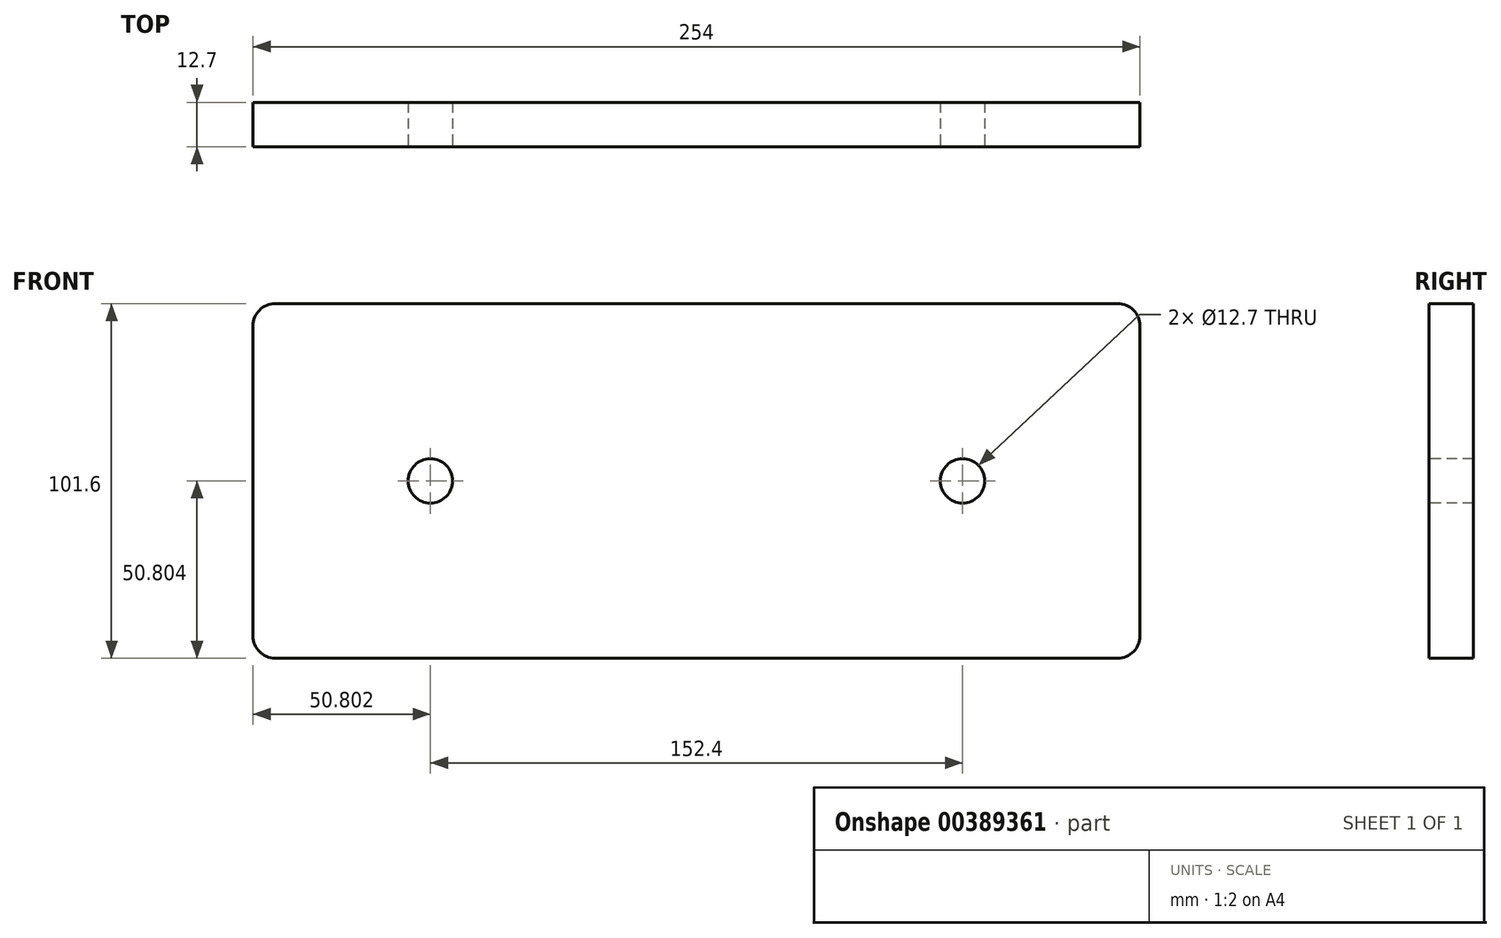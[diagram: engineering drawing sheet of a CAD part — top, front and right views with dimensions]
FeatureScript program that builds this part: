
annotation { "Feature Type Name" : "Feature", "Feature Type Description" : "" }
export const myFeature = defineFeature(function(context is Context, id is Id, definition is map)
    precondition{}
    {
        {
            var Q0;
            Q0=qCreatedBy(makeId("Front.planeOp"),FACE);
            var sketch = newSketch(context, id + "F0", { "sketchPlane" : qUnion([Q0])});
            skLineSegment(sketch, "E0.bottom", {"start": v(-166.69, 61.21) * mm, "end": v(74.61, 61.21) * mm});
            skLineSegment(sketch, "E0.top", {"start": v(-166.69, -40.39) * mm, "end": v(74.61, -40.39) * mm});
            skLineSegment(sketch, "E0.left", {"start": v(-173.04, 54.86) * mm, "end": v(-173.04, -34.04) * mm});
            skLineSegment(sketch, "E0.right", {"start": v(80.96, 54.86) * mm, "end": v(80.96, -34.04) * mm});
            skPoint(sketch, "E1.visualSharp", {"position": v(-173.04, 61.21) * mm});
            skArc(sketch, "E1.filletArc", {"start": v(-166.69, 61.21) * mm, "mid": v(-171.18, 59.35) * mm, "end": v(-173.04, 54.86) * mm});
            skPoint(sketch, "E2.visualSharp", {"position": v(80.96, 61.21) * mm});
            skArc(sketch, "E2.filletArc", {"start": v(80.96, 54.86) * mm, "mid": v(79.1, 59.35) * mm, "end": v(74.61, 61.21) * mm});
            skPoint(sketch, "E3.visualSharp", {"position": v(80.96, -40.39) * mm});
            skArc(sketch, "E3.filletArc", {"start": v(74.61, -40.39) * mm, "mid": v(79.1, -38.53) * mm, "end": v(80.96, -34.04) * mm});
            skPoint(sketch, "E4.visualSharp", {"position": v(-173.04, -40.39) * mm});
            skArc(sketch, "E4.filletArc", {"start": v(-173.04, -34.04) * mm, "mid": v(-171.18, -38.53) * mm, "end": v(-166.69, -40.39) * mm});
            skSolve(sketch);
        }
        {
            var Q0;
            Q0 = qSketchRegion(id + "F0", true);
            extrude(context, id + "F1", {"entities" : qUnion([Q0]), "depth" : 12.7 * mm});
        }
        {
            var Q0;
            Q0=makeQuery(id+"F1.opExtrude","CAP_FACE",FACE,{"disambiguationData":[OSD([sQuery(id+"F0.wireOp",EDGE,"E0.bottom"),sQuery(id+"F0.wireOp",EDGE,"E0.top"),sQuery(id+"F0.wireOp",EDGE,"E0.left"),sQuery(id+"F0.wireOp",EDGE,"E0.right"),sQuery(id+"F0.wireOp",EDGE,"E1.filletArc"),sQuery(id+"F0.wireOp",EDGE,"E2.filletArc"),sQuery(id+"F0.wireOp",EDGE,"E3.filletArc"),sQuery(id+"F0.wireOp",EDGE,"E4.filletArc")])],"isStart":false});
            var sketch = newSketch(context, id + "F2", { "sketchPlane" : qUnion([Q0])});
            skCircle(sketch, "E5", {"center": v(-122.24, 10.41) * mm, "radius": 6.35 * mm});
            skLineSegment(sketch, "E6", {"start": v(-46.04, 61.21) * mm, "end": v(-46.04, -40.39) * mm, "construction": true});
            skCircle(sketch, "E7", {"center": v(30.16, 10.41) * mm, "radius": 6.35 * mm});
            skSolve(sketch);
        }
        {
            var Q0;
            Q0=sQuery(id+"F2.wireOp",VERTEX,"E5.center");
            var Q1;
            Q1=sQuery(id+"F2.wireOp",VERTEX,"E7.center");
            var Q2;
            Q2=makeQuery(id+"F1.opExtrude","SWEPT_BODY",BODY,{"disambiguationData":[OSD([sQuery(id+"F0.wireOp",EDGE,"E0.bottom"),sQuery(id+"F0.wireOp",EDGE,"E0.top"),sQuery(id+"F0.wireOp",EDGE,"E0.left"),sQuery(id+"F0.wireOp",EDGE,"E0.right"),sQuery(id+"F0.wireOp",EDGE,"E1.filletArc"),sQuery(id+"F0.wireOp",EDGE,"E2.filletArc"),sQuery(id+"F0.wireOp",EDGE,"E3.filletArc"),sQuery(id+"F0.wireOp",EDGE,"E4.filletArc")])]});
            hole(context, id + "F3", {"style" : HoleStyle.SIMPLE, "endStyle" : HoleEndStyle.BLIND, "holeDiameter" : 12.7 * mm, "holeDepth" : 12.7 * mm, "isTappedThrough" : true, "tappedDepth" : 12.7 * mm, "tapClearance" : 3, "locations" : qUnion([Q0, Q1]), "scope" : qUnion([Q2])});
        }
    });
